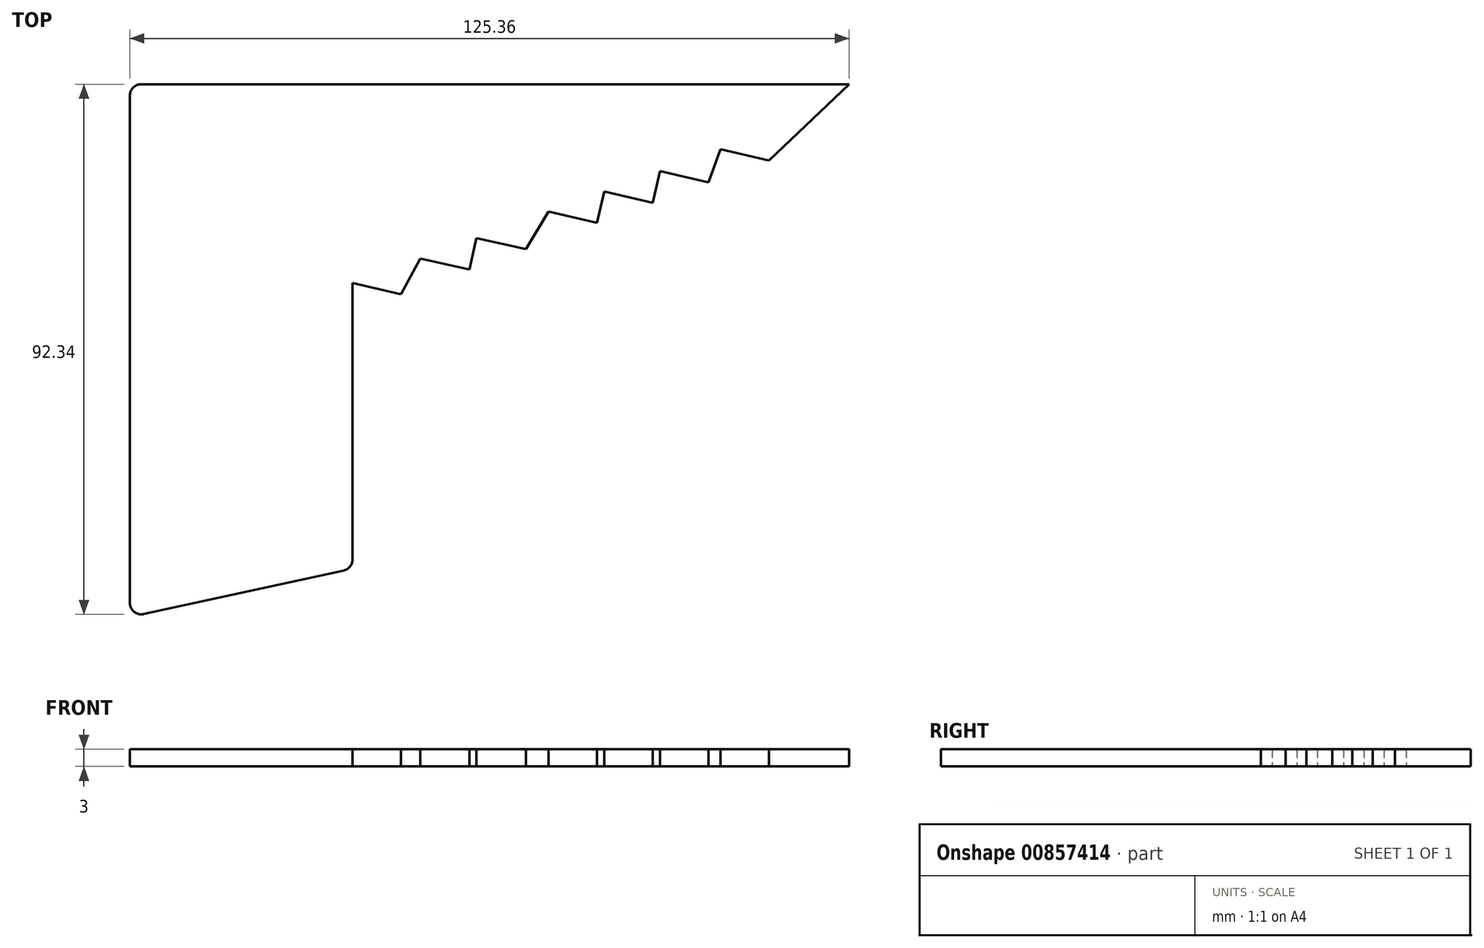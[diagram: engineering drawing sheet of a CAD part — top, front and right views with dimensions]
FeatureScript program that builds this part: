
annotation { "Feature Type Name" : "Feature", "Feature Type Description" : "" }
export const myFeature = defineFeature(function(context is Context, id is Id, definition is map)
    precondition{}
    {
        {
            var Q0;
            Q0=qCreatedBy(makeId("Top.planeOp"),FACE);
            var sketch = newSketch(context, id + "F0", { "sketchPlane" : qUnion([Q0])});
            skLineSegment(sketch, "E0", {"start": v(-76.13, 76.85) * mm, "end": v(44.87, 76.85) * mm});
            skLineSegment(sketch, "E1", {"start": v(44.87, 76.85) * mm, "end": v(47.23, 76.85) * mm});
            skLineSegment(sketch, "E2", {"start": v(47.23, 76.85) * mm, "end": v(33.24, 63.6) * mm});
            skLineSegment(sketch, "E3", {"start": v(-39.3, 36.07) * mm, "end": v(-39.3, -5.9) * mm});
            skLineSegment(sketch, "E4", {"start": v(-40.88, -7.85) * mm, "end": v(-75.7, -15.44) * mm});
            skLineSegment(sketch, "E5", {"start": v(-78.13, -13.49) * mm, "end": v(-78.13, 74.85) * mm});
            skPoint(sketch, "E6.visualSharp", {"position": v(-78.13, 76.85) * mm});
            skArc(sketch, "E6.filletArc", {"start": v(-76.13, 76.85) * mm, "mid": v(-77.55, 76.27) * mm, "end": v(-78.13, 74.85) * mm});
            skPoint(sketch, "E7.visualSharp", {"position": v(-39.3, -7.5) * mm});
            skArc(sketch, "E7.filletArc", {"start": v(-40.88, -7.85) * mm, "mid": v(-39.75, -7.15) * mm, "end": v(-39.3, -5.9) * mm});
            skPoint(sketch, "E8.visualSharp", {"position": v(-78.13, -15.97) * mm});
            skArc(sketch, "E8.filletArc", {"start": v(-78.13, -13.49) * mm, "mid": v(-77.39, -15.05) * mm, "end": v(-75.7, -15.44) * mm});
            skLineSegment(sketch, "E9", {"start": v(33.24, 63.6) * mm, "end": v(24.82, 65.57) * mm});
            skLineSegment(sketch, "E10", {"start": v(24.82, 65.57) * mm, "end": v(22.68, 59.75) * mm});
            skLineSegment(sketch, "E11", {"start": v(22.68, 59.75) * mm, "end": v(14.26, 61.72) * mm});
            skLineSegment(sketch, "E12", {"start": v(14.26, 61.72) * mm, "end": v(12.97, 56.22) * mm});
            skLineSegment(sketch, "E13", {"start": v(12.97, 56.22) * mm, "end": v(4.55, 58.19) * mm});
            skLineSegment(sketch, "E14", {"start": v(4.55, 58.19) * mm, "end": v(3.26, 52.68) * mm});
            skLineSegment(sketch, "E15", {"start": v(3.26, 52.68) * mm, "end": v(-5.16, 54.66) * mm});
            skLineSegment(sketch, "E16", {"start": v(-5.16, 54.66) * mm, "end": v(-9.13, 48.17) * mm});
            skLineSegment(sketch, "E17", {"start": v(-9.13, 48.17) * mm, "end": v(-17.76, 50.07) * mm});
            skLineSegment(sketch, "E18", {"start": v(-17.76, 50.07) * mm, "end": v(-18.96, 44.6) * mm});
            skLineSegment(sketch, "E19", {"start": v(-18.96, 44.6) * mm, "end": v(-27.52, 46.52) * mm});
            skLineSegment(sketch, "E20", {"start": v(-27.52, 46.52) * mm, "end": v(-30.89, 40.25) * mm});
            skLineSegment(sketch, "E21", {"start": v(-30.89, 40.25) * mm, "end": v(-39.3, 42.23) * mm});
            skLineSegment(sketch, "E22", {"start": v(-39.3, 42.23) * mm, "end": v(-39.3, 36.07) * mm});
            skLineSegment(sketch, "E23", {"start": v(-39.3, 42.23) * mm, "end": v(24.82, 65.57) * mm, "construction": true});
            skLineSegment(sketch, "E24", {"start": v(-30.89, 40.25) * mm, "end": v(33.24, 63.6) * mm, "construction": true});
            skSolve(sketch);
        }
        {
            var Q0;
            Q0 = qSketchRegion(id + "F0", true);
            extrude(context, id + "F1", {"entities" : qUnion([Q0]), "depth" : 3 * mm, "offsetDistance" : 25 * mm});
        }
    });
